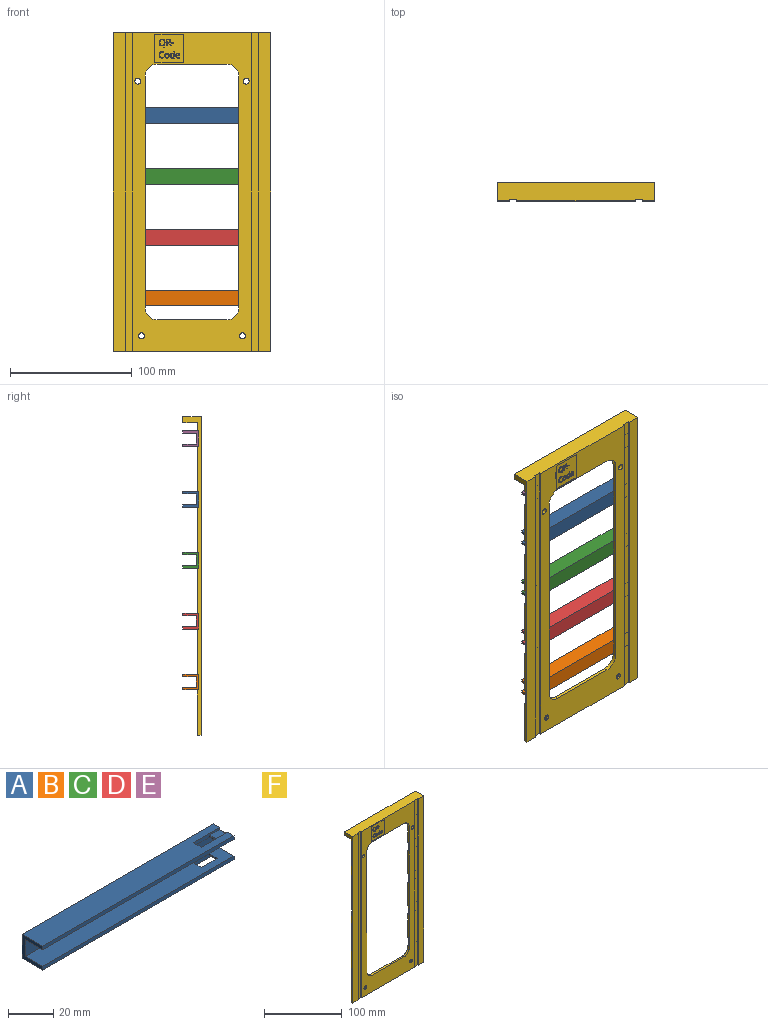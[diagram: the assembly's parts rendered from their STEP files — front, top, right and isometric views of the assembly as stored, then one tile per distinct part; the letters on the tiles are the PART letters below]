
ASSEMBLY  parts=6 mates=5
PART A: 24 faces, bbox 120x13x13 mm
  f0: plane 120x13mm, normal (0,0,-1), area 1477.5mm2, adj f3,f6,f7,f8,f13,f14,f16
  f1: plane 120x11mm, normal (0,0,-1), area 1270mm2, adj f3,f5,f6,f9,f10,f11,f18,f19
  f2: plane 120x11mm, normal (0,0,1), area 1270mm2, adj f3,f6,f7,f9,f13,f14,f16,f17
  f3: plane 13x13mm, normal (1,0,0), area 57mm2, adj f0,f1,f2,f4,f5,f7,f8,f9
  f4: plane 120x13mm, normal (0,0,1), area 1477.5mm2, adj f3,f5,f6,f8,f10,f11,f19
  f5: plane 120x2mm, normal (0,-1,0), area 240mm2, adj f1,f3,f4,f6
  f6: plane 13x13mm, normal (-1,0,0), area 70mm2, adj f0,f1,f2,f4,f5,f7,f8,f9
  f7: plane 120x2mm, normal (0,-1,0), area 240mm2, adj f0,f2,f3,f6
  f8: plane 120x13mm, normal (0,1,0), area 1560mm2, adj f0,f3,f4,f6
  f9: plane 120x9mm, normal (0,-1,0), area 1080mm2, adj f1,f2,f3,f6
  f10: plane 16.5x2mm, normal (0,-1,0), area 26.5mm2, adj f1,f3,f4,f12,f18,f19,f21,f23
  f11: plane 16.5x2mm, normal (0,1,0), area 26.5mm2, adj f1,f3,f4,f12,f18,f19,f21,f23
  f12: plane 5.9x5mm, normal (0,0,1), area 29.5mm2, adj f10,f11,f21,f23
  f13: plane 16.5x2mm, normal (0,1,0), area 26.5mm2, adj f0,f2,f3,f15,f16,f17,f20,f22
  f14: plane 16.5x2mm, normal (0,-1,0), area 26.5mm2, adj f0,f2,f3,f15,f16,f17,f20,f22
  f15: plane 5.9x5mm, normal (0,0,-1), area 29.5mm2, adj f13,f14,f20,f22
  f16: plane 5x2mm, normal (1,0,0), area 10mm2, adj f0,f2,f13,f14
  f17: plane 5x0.7mm, normal (-1,0,0), area 3.5mm2, adj f2,f13,f14,f20
  f18: plane 5x0.7mm, normal (-1,0,0), area 3.5mm2, adj f1,f10,f11,f21
  f19: plane 5x2mm, normal (1,0,0), area 10mm2, adj f1,f4,f10,f11
  f20: cylinder r=0.3mm len=5mm, axis (0,1,0), area 2.4mm2, adj f13,f14,f15,f17
  f21: cylinder r=0.3mm len=5mm, axis (0,-1,0), area 2.4mm2, adj f10,f11,f12,f18
  f22: cylinder r=0.3mm len=5mm, axis (0,1,0), area 2.4mm2, adj f3,f13,f14,f15
  f23: cylinder r=0.3mm len=5mm, axis (0,1,0), area 2.4mm2, adj f3,f10,f11,f12
PART B: same geometry as A
PART C: same geometry as A
PART D: same geometry as A
PART E: same geometry as A
PART F: 201 faces, bbox 129x15x262 mm
  f0: plane 23.5x23.5mm, normal (0,-1,0), area 475.6mm2, adj f68,f69,f70,f71,f72,f73,f74,f75
  f1: plane 262x97mm, normal (0,-1,0), area 8705.2mm2, adj f3,f4,f5,f14,f15,f19,f20,f21
  f2: plane 262x10mm, normal (0,-1,0), area 2620mm2, adj f3,f16,f19,f66
  f3: plane 129x15mm, normal (0,0,1), area 1919.4mm2, adj f1,f2,f16,f18,f28,f29,f62,f63
  f4: cylinder r=2.4mm len=4.8mm, axis (0,1,0), area 27.1mm2, adj f1,f61
  f5: cylinder r=2.4mm len=4.8mm, axis (0,1,0), area 27.1mm2, adj f1,f59
  f6: plane 129x37mm, normal (0,1,0), area 2038.5mm2, adj f14,f15,f16,f18,f21,f22,f23,f26
  f7: plane 129x37.4mm, normal (0,1,0), area 3933.2mm2, adj f14,f15,f16,f18,f19,f20,f24,f25
  f8: plane 37x26mm, normal (0,1,0), area 962mm2, adj f15,f16,f38,f42
  f9: plane 37x26mm, normal (0,1,0), area 962mm2, adj f14,f18,f53,f55
  f10: plane 37x26mm, normal (0,1,0), area 962mm2, adj f15,f16,f35,f39
  f11: plane 37x26mm, normal (0,1,0), area 962mm2, adj f14,f18,f50,f52
  f12: plane 37x26mm, normal (0,1,0), area 962mm2, adj f15,f16,f32,f36
  f13: plane 37x26mm, normal (0,1,0), area 962mm2, adj f14,f18,f47,f49
  f14: plane 190x3mm, normal (1,0,0), area 518mm2, adj f1,f6,f7,f9,f11,f13,f20,f21
  f15: plane 190x3mm, normal (-1,0,0), area 518mm2, adj f1,f6,f7,f8,f10,f12,f23,f24
  f16: plane 262x15mm, normal (1,0,0), area 781mm2, adj f2,f3,f6,f7,f8,f10,f12,f17
  f17: plane 129x6.6mm, normal (0,1,0), area 851.4mm2, adj f16,f18,f30,f43
  f18: plane 262x15mm, normal (-1,0,0), area 781mm2, adj f3,f6,f7,f9,f11,f13,f17,f19
  f19: plane 129x3mm, normal (0,0,-1), area 371.4mm2, adj f1,f2,f7,f16,f18,f28,f62,f63
  f20: cylinder r=10mm len=10mm, axis (0,1,0), area 47.1mm2, adj f1,f7,f14,f25
  f21: cylinder r=10mm len=10mm, axis (0,1,0), area 47.1mm2, adj f1,f6,f14,f22
  f22: plane 57x3mm, normal (0,0,-1), area 171mm2, adj f1,f6,f21,f23
  f23: cylinder r=10mm len=10mm, axis (0,1,0), area 47.1mm2, adj f1,f6,f15,f22
  f24: cylinder r=10mm len=10mm, axis (0,1,0), area 47.1mm2, adj f1,f7,f15,f25
  f25: plane 57x3mm, normal (0,0,1), area 171mm2, adj f1,f7,f20,f24
  f26: cylinder r=2.4mm len=4.8mm, axis (0,1,0), area 45.2mm2, adj f1,f6
  f27: cylinder r=2.4mm len=4.8mm, axis (0,1,0), area 45.2mm2, adj f1,f6
  f28: plane 262x10mm, normal (0,-1,0), area 2620mm2, adj f3,f18,f19,f62
  f29: plane 129x5mm, normal (0,1,0), area 645mm2, adj f3,f16,f18,f30
  f30: plane 129x12mm, normal (0,0,-1), area 1548mm2, adj f16,f17,f18,f29
  f31: plane 26x13mm, normal (0,1,0), area 338mm2, adj f15,f16,f32,f33
  f32: plane 26x1mm, normal (0,0,1), area 26mm2, adj f12,f15,f16,f31
  f33: plane 26x1mm, normal (0,0,-1), area 26mm2, adj f6,f15,f16,f31
  f34: plane 26x13mm, normal (0,1,0), area 338mm2, adj f15,f16,f35,f36
  f35: plane 26x1mm, normal (0,0,1), area 26mm2, adj f10,f15,f16,f34
  f36: plane 26x1mm, normal (0,0,-1), area 26mm2, adj f12,f15,f16,f34
  f37: plane 26x13mm, normal (0,1,0), area 338mm2, adj f15,f16,f38,f39
  f38: plane 26x1mm, normal (0,0,1), area 26mm2, adj f8,f15,f16,f37
  f39: plane 26x1mm, normal (0,0,-1), area 26mm2, adj f10,f15,f16,f37
  f40: plane 26x13mm, normal (0,1,0), area 338mm2, adj f15,f16,f41,f42
  f41: plane 26x1mm, normal (0,0,1), area 26mm2, adj f7,f15,f16,f40
  f42: plane 26x1mm, normal (0,0,-1), area 26mm2, adj f8,f15,f16,f40
  f43: plane 129x1mm, normal (0,0,-1), area 129mm2, adj f16,f17,f18,f45
  f44: plane 129x1mm, normal (0,0,1), area 129mm2, adj f6,f16,f18,f45
  f45: plane 129x13mm, normal (0,1,0), area 1677mm2, adj f16,f18,f43,f44
  f46: plane 26x1mm, normal (0,0,-1), area 26mm2, adj f6,f14,f18,f48
  f47: plane 26x1mm, normal (0,0,1), area 26mm2, adj f13,f14,f18,f48
  f48: plane 26x13mm, normal (0,1,0), area 338mm2, adj f14,f18,f46,f47
  f49: plane 26x1mm, normal (0,0,-1), area 26mm2, adj f13,f14,f18,f51
  f50: plane 26x1mm, normal (0,0,1), area 26mm2, adj f11,f14,f18,f51
  f51: plane 26x13mm, normal (0,1,0), area 338mm2, adj f14,f18,f49,f50
  f52: plane 26x1mm, normal (0,0,-1), area 26mm2, adj f11,f14,f18,f54
  f53: plane 26x1mm, normal (0,0,1), area 26mm2, adj f9,f14,f18,f54
  f54: plane 26x13mm, normal (0,1,0), area 338mm2, adj f14,f18,f52,f53
  f55: plane 26x1mm, normal (0,0,-1), area 26mm2, adj f9,f14,f18,f57
  f56: plane 26x1mm, normal (0,0,1), area 26mm2, adj f7,f14,f18,f57
  f57: plane 26x13mm, normal (0,1,0), area 338mm2, adj f14,f18,f55,f56
  f58: cylinder r=3mm len=6mm, axis (0,1,0), area 22.6mm2, adj f7,f59
  f59: plane 6x6mm, normal (0,1,0), area 10.2mm2, adj f5,f58
  f60: cylinder r=3mm len=6mm, axis (0,1,0), area 22.6mm2, adj f7,f61
  f61: plane 6x6mm, normal (0,1,0), area 10.2mm2, adj f4,f60
  f62: plane 262x1.3mm, normal (1,0,0), area 340.6mm2, adj f3,f19,f28,f64
  f63: plane 262x1.3mm, normal (-1,0,0), area 340.6mm2, adj f1,f3,f19,f64
  f64: plane 262x6mm, normal (0,-1,0), area 1572mm2, adj f3,f19,f62,f63
  f65: plane 262x1.3mm, normal (1,0,0), area 340.6mm2, adj f1,f3,f19,f67
  f66: plane 262x1.3mm, normal (-1,0,0), area 340.6mm2, adj f2,f3,f19,f67
  f67: plane 262x6mm, normal (0,-1,0), area 1572mm2, adj f3,f19,f65,f66
  f68: plane 23.5x0.5mm, normal (0,0,-1), area 11.7mm2, adj f0,f1,f69,f71
  f69: plane 23.5x0.5mm, normal (1,0,0), area 11.8mm2, adj f0,f1,f68,f70
  f70: plane 23.5x0.5mm, normal (0,0,1), area 11.7mm2, adj f0,f1,f69,f71
  f71: plane 23.5x0.5mm, normal (-1,0,0), area 11.8mm2, adj f0,f1,f68,f70
  f72: plane 0.55x0.5mm, normal (1,0,0), area 0.3mm2, adj f0,f73,f75,f76
  f73: plane 1.78x0.5mm, normal (0,0,1), area 0.9mm2, adj f0,f72,f74,f76
  f74: plane 0.55x0.5mm, normal (-1,0,0), area 0.3mm2, adj f0,f73,f75,f76
  f75: plane 1.78x0.5mm, normal (0,0,-1), area 0.9mm2, adj f0,f72,f74,f76
  f76: plane 1.78x0.55mm, normal (0,-1,0), area 1mm2, adj f72,f73,f74,f75
  f77: extruded ~0.76x0.5mm, area 0.4mm2, adj f78,f95,f96,f196
  f78: extruded ~0.73x0.5mm, area 0.4mm2, adj f77,f79,f96,f196
  f79: extruded ~0.87x0.5mm, area 0.5mm2, adj f78,f80,f96,f196
  f80: plane 2.08x0.5mm, normal (0,0,-1), area 1mm2, adj f79,f95,f96,f196
  f81: extruded ~1.39x0.54mm, area 0.8mm2, adj f0,f82,f94,f96
  f82: extruded ~0.69x0.5mm, area 0.3mm2, adj f0,f81,f83,f96
  f83: extruded ~0.6x0.5mm, area 0.3mm2, adj f0,f82,f84,f96
  f84: plane 0.54x0.5mm, normal (-1,0,0), area 0.3mm2, adj f0,f83,f85,f96
  f85: extruded ~1.27x0.5mm, area 0.7mm2, adj f0,f84,f86,f96
  f86: extruded ~0.95x0.5mm, area 0.5mm2, adj f0,f85,f87,f96
  f87: extruded ~1.06x0.5mm, area 0.6mm2, adj f0,f86,f88,f96
  f88: plane 2.74x0.5mm, normal (0,0,1), area 1.4mm2, adj f0,f87,f89,f96
  f89: plane 0.5x0.38mm, normal (-1,0,0), area 0.2mm2, adj f0,f88,f90,f96
  f90: extruded ~1.3x0.5mm, area 0.7mm2, adj f0,f89,f91,f96
  f91: extruded ~1.18x0.5mm, area 0.7mm2, adj f0,f90,f92,f96
  f92: extruded ~1.27x0.57mm, area 0.7mm2, adj f0,f91,f93,f96
  f93: extruded ~1.53x0.5mm, area 0.8mm2, adj f0,f92,f94,f96
  f94: extruded ~1.49x0.51mm, area 0.8mm2, adj f0,f81,f93,f96
  f95: extruded ~0.86x0.5mm, area 0.5mm2, adj f77,f80,f96,f196
  f96: plane 4.12x3.37mm, normal (0,-1,0), area 6.3mm2, adj f77,f78,f79,f80,f81,f82,f83,f84
  f97: extruded ~0.89x0.5mm, area 0.5mm2, adj f98,f120,f121,f197
  f98: extruded ~0.82x0.5mm, area 0.5mm2, adj f97,f99,f121,f197
  f99: extruded ~1.15x0.5mm, area 0.6mm2, adj f98,f100,f121,f197
  f100: extruded ~1.16x0.5mm, area 0.6mm2, adj f99,f101,f121,f197
  f101: extruded ~0.81x0.5mm, area 0.5mm2, adj f100,f102,f121,f197
  f102: extruded ~0.9x0.5mm, area 0.5mm2, adj f101,f103,f121,f197
  f103: extruded ~1.21x0.5mm, area 0.6mm2, adj f102,f104,f121,f197
  f104: plane 0.5x0.13mm, normal (1,0,0), area 0.1mm2, adj f103,f120,f121,f197
  f105: plane 0.5x0.03mm, normal (0,0,1), area 0mm2, adj f0,f106,f119,f121
  f106: plane 0.53x0.5mm, normal (0.99,0,0.15), area 0.3mm2, adj f0,f105,f107,f121
  f107: plane 0.5x0.49mm, normal (0,0,1), area 0.2mm2, adj f0,f106,f108,f121
  f108: plane 5.65x0.5mm, normal (-1,0,0), area 2.8mm2, adj f0,f107,f109,f121
  f109: plane 0.6x0.5mm, normal (0,0,-1), area 0.3mm2, adj f0,f108,f110,f121
  f110: plane 1.62x0.5mm, normal (1,0,0), area 0.8mm2, adj f0,f109,f111,f121
  f111: plane 0.5x0.28mm, normal (1,0,0.05), area 0.1mm2, adj f0,f110,f112,f121
  f112: plane 0.5x0.29mm, normal (1,0,0.09), area 0.1mm2, adj f0,f111,f113,f121
  f113: plane 0.5x0.05mm, normal (0,0,-1), area 0mm2, adj f0,f112,f114,f121
  f114: extruded ~1.24x0.59mm, area 0.7mm2, adj f0,f113,f115,f121
  f115: extruded ~1.21x0.54mm, area 0.7mm2, adj f0,f114,f116,f121
  f116: extruded ~1.53x0.5mm, area 0.8mm2, adj f0,f115,f117,f121
  f117: extruded ~1.52x0.5mm, area 0.8mm2, adj f0,f116,f118,f121
  f118: extruded ~1.21x0.53mm, area 0.7mm2, adj f0,f117,f119,f121
  f119: extruded ~1.25x0.61mm, area 0.7mm2, adj f0,f105,f118,f121
  f120: extruded ~1.08x0.5mm, area 0.6mm2, adj f97,f104,f121,f197
  f121: plane 5.72x3.5mm, normal (0,-1,0), area 7.7mm2, adj f97,f98,f99,f100,f101,f102,f103,f104
  f122: extruded ~1.38x0.58mm, area 0.8mm2, adj f0,f123,f136,f137
  f123: extruded ~1.21x0.5mm, area 0.6mm2, adj f0,f122,f124,f137
  f124: plane 0.53x0.5mm, normal (-0.9,0,0.44), area 0.3mm2, adj f0,f123,f125,f137
  f125: extruded ~1.46x0.5mm, area 0.8mm2, adj f0,f124,f126,f137
  f126: extruded ~1.36x0.5mm, area 0.7mm2, adj f0,f125,f127,f137
  f127: extruded ~0.95x0.89mm, area 0.7mm2, adj f0,f126,f128,f137
  f128: extruded ~1.44x0.5mm, area 0.7mm2, adj f0,f127,f129,f137
  f129: extruded ~2.02x0.64mm, area 1.1mm2, adj f0,f128,f130,f137
  f130: extruded ~1.81x0.71mm, area 1mm2, adj f0,f129,f131,f137
  f131: extruded ~1.36x0.5mm, area 0.7mm2, adj f0,f130,f132,f137
  f132: plane 0.54x0.5mm, normal (-1,0,0), area 0.3mm2, adj f0,f131,f133,f137
  f133: extruded ~1.27x0.5mm, area 0.6mm2, adj f0,f132,f134,f137
  f134: extruded ~1.39x0.57mm, area 0.8mm2, adj f0,f133,f135,f137
  f135: extruded ~1.61x0.5mm, area 0.9mm2, adj f0,f134,f136,f137
  f136: extruded ~1.6x0.51mm, area 0.9mm2, adj f0,f122,f135,f137
  f137: plane 5.46x4.01mm, normal (0,-1,0), area 6.2mm2, adj f122,f123,f124,f125,f126,f127,f128,f129
  f138: extruded ~1.64x0.5mm, area 0.9mm2, adj f139,f157,f158,f198
  f139: extruded ~1.62x0.5mm, area 0.9mm2, adj f138,f140,f158,f198
  f140: extruded ~1.34x0.56mm, area 0.8mm2, adj f139,f141,f158,f198
  f141: extruded ~1.33x0.55mm, area 0.7mm2, adj f140,f142,f158,f198
  f142: extruded ~1.62x0.5mm, area 0.9mm2, adj f141,f143,f158,f198
  f143: extruded ~1.64x0.5mm, area 0.9mm2, adj f142,f144,f158,f198
  f144: extruded ~1.33x0.56mm, area 0.7mm2, adj f143,f157,f158,f198
  f145: extruded ~1.7x0.5mm, area 0.9mm2, adj f0,f146,f156,f158
  f146: extruded ~2x0.64mm, area 1.1mm2, adj f0,f145,f147,f158
  f147: extruded ~1.79x0.73mm, area 1mm2, adj f0,f146,f148,f158
  f148: extruded ~1.81x0.71mm, area 1mm2, adj f0,f147,f149,f158
  f149: extruded ~2.01x0.64mm, area 1.1mm2, adj f0,f148,f150,f158
  f150: extruded ~2.02x0.64mm, area 1.1mm2, adj f0,f149,f151,f158
  f151: extruded ~1.81x0.72mm, area 1mm2, adj f0,f150,f152,f158
  f152: plane 0.5x0.2mm, normal (-0.04,0,1), area 0.1mm2, adj f0,f151,f153,f158
  f153: plane 1.2x1.03mm, normal (0.76,0,0.65), area 0.8mm2, adj f0,f152,f154,f158
  f154: plane 0.9x0.5mm, normal (0,0,1), area 0.4mm2, adj f0,f153,f155,f158
  f155: plane 1.32x1.26mm, normal (-0.72,0,-0.69), area 0.9mm2, adj f0,f154,f156,f158
  f156: extruded ~1.16x0.91mm, area 0.8mm2, adj f0,f145,f155,f158
  f157: extruded ~1.33x0.56mm, area 0.7mm2, adj f138,f144,f158,f198
  f158: plane 6.65x4.88mm, normal (0,-1,0), area 10mm2, adj f138,f139,f140,f141,f142,f143,f144,f145
  f159: plane 0.85x0.5mm, normal (0,0,-1), area 0.4mm2, adj f160,f176,f177,f199
  f160: plane 2.03x0.5mm, normal (-1,0,0), area 1mm2, adj f159,f161,f177,f199
  f161: plane 0.8x0.5mm, normal (0,0,1), area 0.4mm2, adj f160,f162,f177,f199
  f162: extruded ~1x0.5mm, area 0.5mm2, adj f161,f163,f177,f199
  f163: extruded ~0.76x0.5mm, area 0.4mm2, adj f162,f164,f177,f199
  f164: extruded ~0.78x0.5mm, area 0.4mm2, adj f163,f176,f177,f199
  f165: plane 2.21x0.5mm, normal (-1,0,0), area 1.1mm2, adj f0,f166,f175,f177
  f166: plane 1.11x0.5mm, normal (0,0,1), area 0.6mm2, adj f0,f165,f167,f177
  f167: plane 2.21x1.28mm, normal (0.86,0,0.5), area 1.3mm2, adj f0,f166,f168,f177
  f168: plane 0.73x0.5mm, normal (0,0,1), area 0.4mm2, adj f0,f167,f169,f177
  f169: plane 2.38x1.44mm, normal (-0.86,0,-0.52), area 1.4mm2, adj f0,f168,f170,f177
  f170: extruded ~1.42x1.07mm, area 1mm2, adj f0,f169,f171,f177
  f171: extruded ~1.13x0.5mm, area 0.6mm2, adj f0,f170,f172,f177
  f172: extruded ~1.44x0.5mm, area 0.8mm2, adj f0,f171,f173,f177
  f173: plane 1.46x0.5mm, normal (0,0,-1), area 0.7mm2, adj f0,f172,f174,f177
  f174: plane 5.31x0.5mm, normal (1,0,0), area 2.7mm2, adj f0,f173,f175,f177
  f175: plane 0.62x0.5mm, normal (0,0,1), area 0.3mm2, adj f0,f165,f174,f177
  f176: extruded ~0.96x0.5mm, area 0.5mm2, adj f159,f164,f177,f199
  f177: plane 5.31x3.74mm, normal (0,-1,0), area 8.4mm2, adj f159,f160,f161,f162,f163,f164,f165,f166
  f178: extruded ~1.16x0.5mm, area 0.6mm2, adj f179,f194,f195,f200
  f179: extruded ~1.16x0.5mm, area 0.6mm2, adj f178,f180,f195,f200
  f180: extruded ~0.89x0.5mm, area 0.5mm2, adj f179,f181,f195,f200
  f181: extruded ~0.91x0.5mm, area 0.5mm2, adj f180,f182,f195,f200
  f182: extruded ~1.15x0.5mm, area 0.6mm2, adj f181,f183,f195,f200
  f183: extruded ~1.16x0.5mm, area 0.6mm2, adj f182,f184,f195,f200
  f184: extruded ~0.9x0.5mm, area 0.5mm2, adj f183,f194,f195,f200
  f185: extruded ~1.52x0.5mm, area 0.8mm2, adj f0,f186,f193,f195
  f186: extruded ~1.5x0.5mm, area 0.8mm2, adj f0,f185,f187,f195
  f187: extruded ~1.33x0.56mm, area 0.7mm2, adj f0,f186,f188,f195
  f188: extruded ~1.35x0.54mm, area 0.8mm2, adj f0,f187,f189,f195
  f189: extruded ~1.52x0.5mm, area 0.8mm2, adj f0,f188,f190,f195
  f190: extruded ~1.1x0.5mm, area 0.6mm2, adj f0,f189,f191,f195
  f191: extruded ~0.72x0.64mm, area 0.5mm2, adj f0,f190,f192,f195
  f192: extruded ~0.95x0.5mm, area 0.5mm2, adj f0,f191,f193,f195
  f193: extruded ~1.35x0.55mm, area 0.8mm2, adj f0,f185,f192,f195
  f194: extruded ~0.9x0.5mm, area 0.5mm2, adj f178,f184,f195,f200
  f195: plane 4.12x3.66mm, normal (0,-1,0), area 6.1mm2, adj f178,f179,f180,f181,f182,f183,f184,f185
  f196: plane 2.08x1.18mm, normal (0,-1,0), area 2mm2, adj f77,f78,f79,f80,f95
  f197: plane 3.11x2.27mm, normal (0,-1,0), area 5.9mm2, adj f97,f98,f99,f100,f101,f102,f103,f104
  f198: plane 4.37x3.58mm, normal (0,-1,0), area 13mm2, adj f138,f139,f140,f141,f142,f143,f144,f157
  f199: plane 2.11x2.03mm, normal (0,-1,0), area 3.9mm2, adj f159,f160,f161,f162,f163,f164,f176
  f200: plane 3.11x2.41mm, normal (0,-1,0), area 6.2mm2, adj f178,f179,f180,f181,f182,f183,f184,f194
PLACE A rot(axis=(1,0,0),180deg) t=(-3.35,2.64,93.21)mm
PLACE B rot(axis=(1,0,0),180deg) t=(-3.35,2.64,-56.79)mm
PLACE C rot(axis=(1,0,0),180deg) t=(-3.35,2.64,43.21)mm
PLACE D rot(axis=(1,0,0),180deg) t=(-3.35,2.64,-6.79)mm
PLACE E rot(axis=(1,0,0),180deg) t=(-3.35,2.64,143.21)mm
PLACE F t=(-9.3,3.64,0.84)mm
MATE fastened A.f4 <-> F.f32  axis (0,0,-1) through (59.66,2.64,72.81)mm
MATE fastened B.f4 <-> F.f41  axis (0,0,-1) through (59.66,2.64,-77.19)mm
MATE fastened C.f4 <-> F.f35  axis (0,0,-1) through (59.66,2.64,22.81)mm
MATE fastened D.f4 <-> F.f38  axis (0,0,-1) through (59.66,2.64,-27.19)mm
MATE fastened E.f4 <-> F.f44  axis (0,0,-1) through (59.66,2.64,122.81)mm
